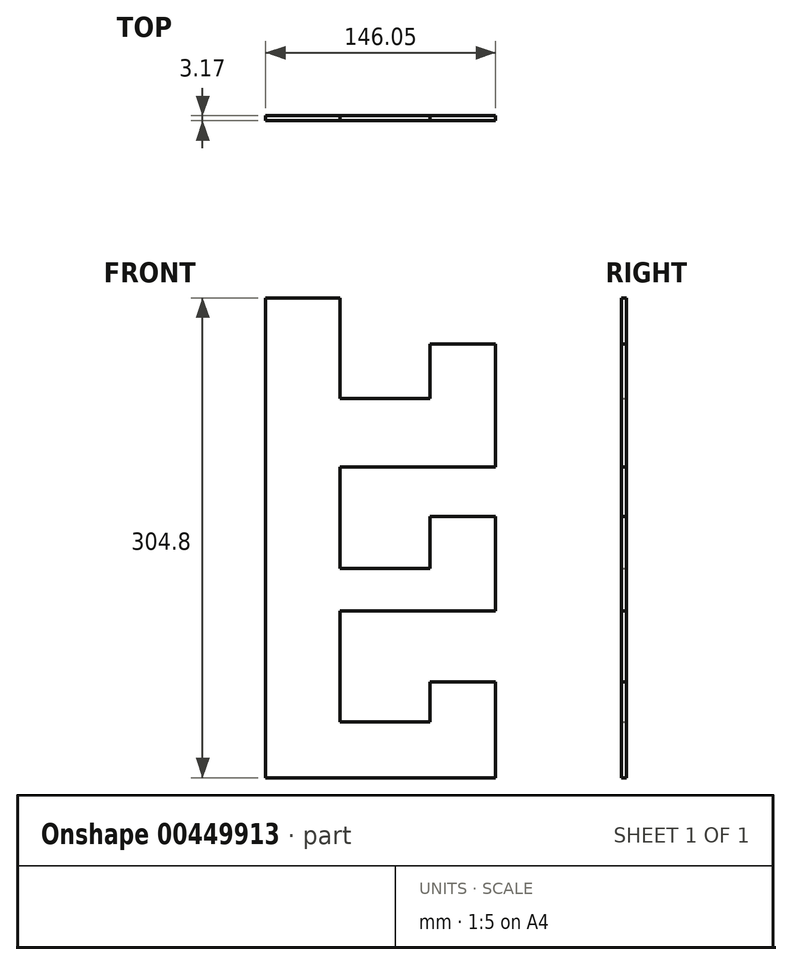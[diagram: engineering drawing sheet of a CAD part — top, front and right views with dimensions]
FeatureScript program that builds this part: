
annotation { "Feature Type Name" : "Feature", "Feature Type Description" : "" }
export const myFeature = defineFeature(function(context is Context, id is Id, definition is map)
    precondition{}
    {
        {
            var Q0;
            Q0=qCreatedBy(makeId("Front.planeOp"),FACE);
            var sketch = newSketch(context, id + "F0", { "sketchPlane" : qUnion([Q0])});
            skLineSegment(sketch, "E0", {"start": v(0, 0) * mm, "end": v(0, 304.8) * mm});
            skLineSegment(sketch, "E1", {"start": v(146.05, 0) * mm, "end": v(0, 0) * mm});
            skLineSegment(sketch, "E2", {"start": v(47.14, 304.8) * mm, "end": v(0, 304.8) * mm});
            skLineSegment(sketch, "E3", {"start": v(47.14, 304.8) * mm, "end": v(47.14, 240.87) * mm});
            skLineSegment(sketch, "E4", {"start": v(47.14, 240.87) * mm, "end": v(104.52, 240.87) * mm});
            skLineSegment(sketch, "E5", {"start": v(104.52, 240.87) * mm, "end": v(104.52, 275.36) * mm});
            skLineSegment(sketch, "E6", {"start": v(104.52, 275.36) * mm, "end": v(146.05, 275.36) * mm});
            skLineSegment(sketch, "E7", {"start": v(146.05, 275.36) * mm, "end": v(146.05, 197.39) * mm});
            skLineSegment(sketch, "E8", {"start": v(146.05, 197.39) * mm, "end": v(47.14, 197.39) * mm});
            skLineSegment(sketch, "E9", {"start": v(47.14, 197.39) * mm, "end": v(47.14, 132.9) * mm});
            skLineSegment(sketch, "E10", {"start": v(47.14, 132.9) * mm, "end": v(104.52, 132.9) * mm});
            skLineSegment(sketch, "E11", {"start": v(104.52, 132.9) * mm, "end": v(104.52, 165.9) * mm});
            skLineSegment(sketch, "E12", {"start": v(104.52, 165.9) * mm, "end": v(146.05, 165.9) * mm});
            skLineSegment(sketch, "E13", {"start": v(146.05, 165.9) * mm, "end": v(146.05, 105.91) * mm});
            skLineSegment(sketch, "E14", {"start": v(146.05, 105.91) * mm, "end": v(47.14, 105.91) * mm});
            skLineSegment(sketch, "E15", {"start": v(47.14, 105.91) * mm, "end": v(47.14, 35.43) * mm});
            skLineSegment(sketch, "E16", {"start": v(47.14, 35.43) * mm, "end": v(104.52, 35.43) * mm});
            skLineSegment(sketch, "E17", {"start": v(104.52, 35.43) * mm, "end": v(104.52, 60.93) * mm});
            skLineSegment(sketch, "E18", {"start": v(104.52, 60.93) * mm, "end": v(146.05, 60.93) * mm});
            skLineSegment(sketch, "E19", {"start": v(146.05, 60.93) * mm, "end": v(146.05, 0) * mm});
            skSolve(sketch);
        }
        {
            var Q0;
            Q0=makeQuery(id+"F0.imprint","IMPRINT",FACE,{"disambiguationData":[TD([[makeQuery(id+"F0.imprint","IMPRINT",EDGE,{"derivedFrom":sQuery(id+"F0.wireOp",EDGE,"E0")}),-1.0]])]});
            extrude(context, id + "F1", {"entities" : qUnion([Q0]), "depth" : 3.17 * mm});
        }
    });
